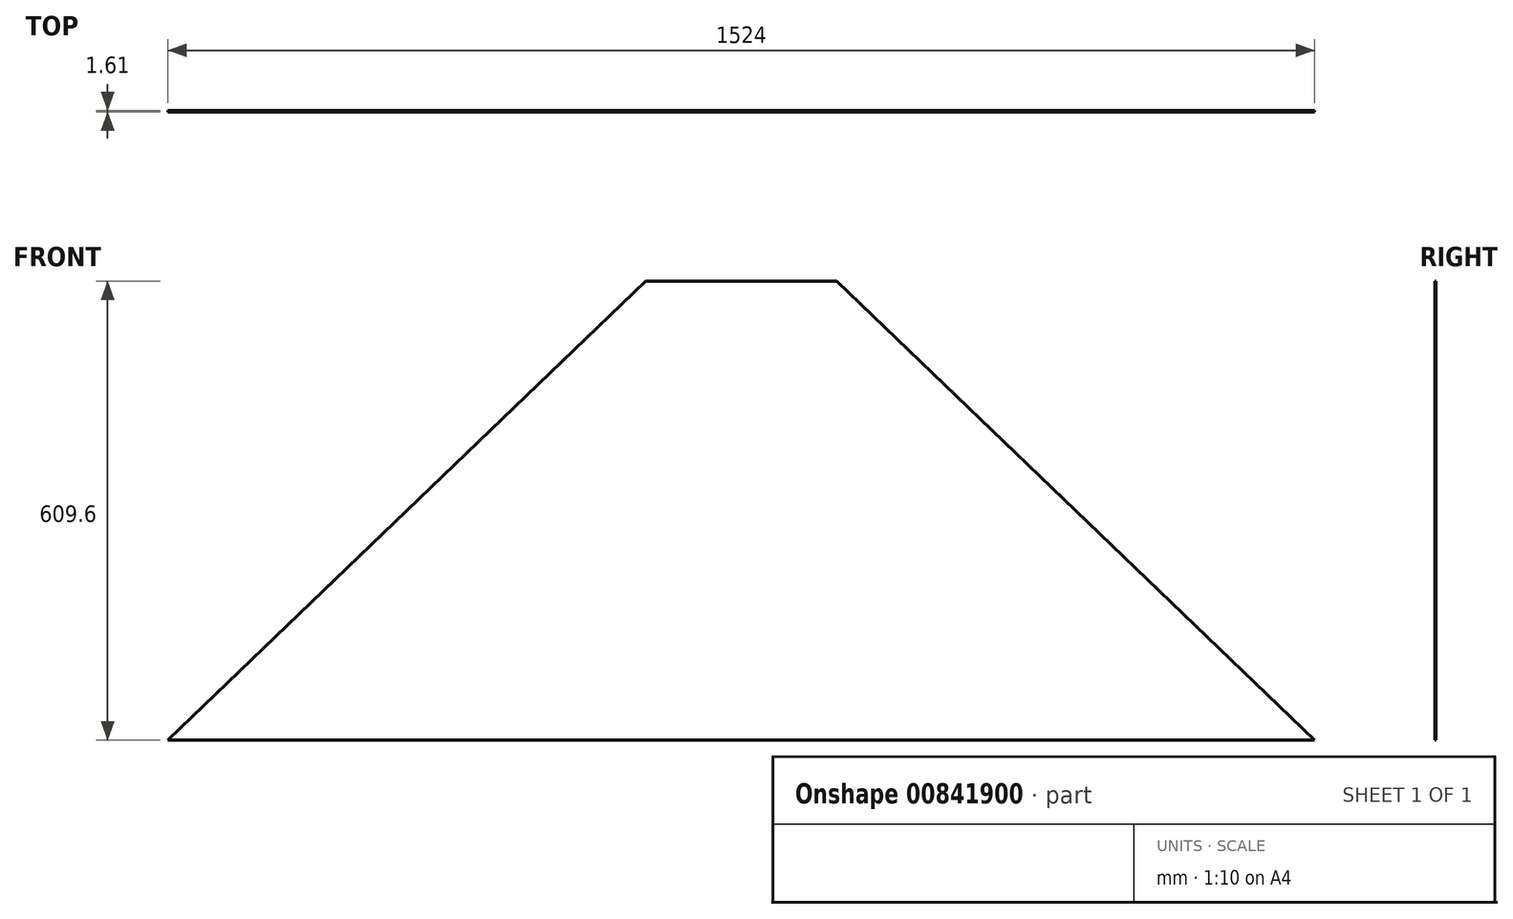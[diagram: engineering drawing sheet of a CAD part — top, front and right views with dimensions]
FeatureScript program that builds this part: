
annotation { "Feature Type Name" : "Feature", "Feature Type Description" : "" }
export const myFeature = defineFeature(function(context is Context, id is Id, definition is map)
    precondition{}
    {
        {
            var Q0;
            Q0=qCreatedBy(makeId("Front.planeOp"),FACE);
            var sketch = newSketch(context, id + "F0", { "sketchPlane" : qUnion([Q0])});
            skLineSegment(sketch, "E0", {"start": v(0, 0) * mm, "end": v(635, 609.6) * mm});
            skLineSegment(sketch, "E1", {"start": v(635, 609.6) * mm, "end": v(889, 609.6) * mm});
            skLineSegment(sketch, "E2", {"start": v(889, 609.6) * mm, "end": v(1524, 0) * mm});
            skLineSegment(sketch, "E3", {"start": v(1524, 0) * mm, "end": v(0, 0) * mm});
            skLineSegment(sketch, "E4", {"start": v(762, 609.6) * mm, "end": v(762, 0) * mm, "construction": true});
            skSolve(sketch);
        }
        {
            var Q0;
            Q0 = qSketchRegion(id + "F0", true);
            extrude(context, id + "F1", {"entities" : qUnion([Q0]), "depth" : 1.61 * mm, "offsetDistance" : 25.4 * mm});
        }
    });
